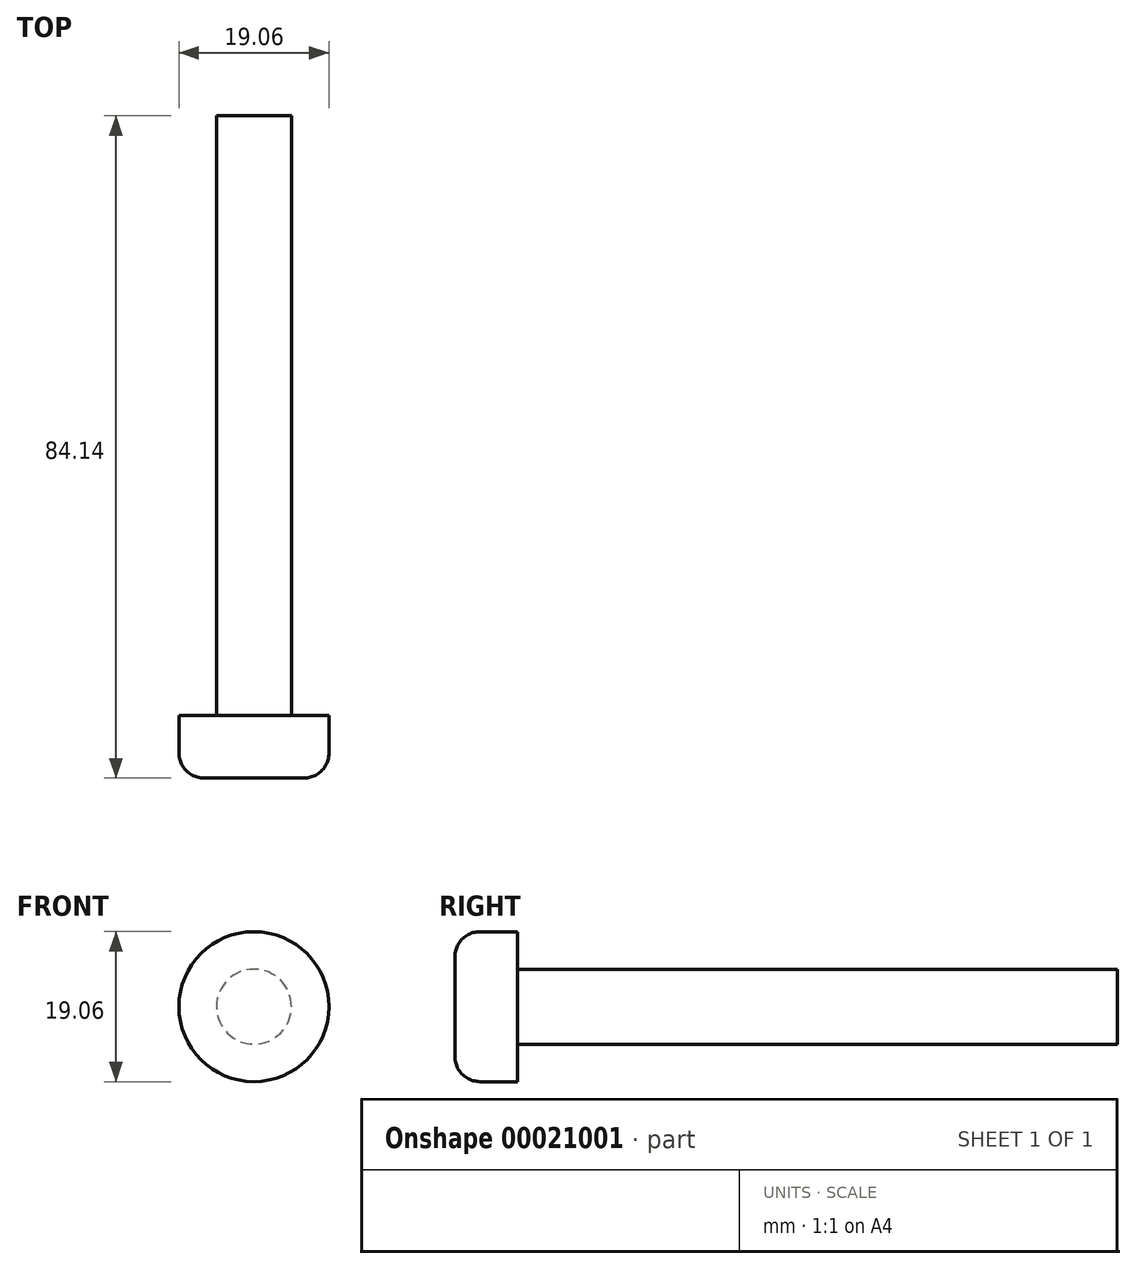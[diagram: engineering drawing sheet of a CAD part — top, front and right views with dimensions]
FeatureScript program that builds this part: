
annotation { "Feature Type Name" : "Feature", "Feature Type Description" : "" }
export const myFeature = defineFeature(function(context is Context, id is Id, definition is map)
    precondition{}
    {
        {
            var Q0;
            Q0=qCreatedBy(makeId("Front.planeOp"),FACE);
            var sketch = newSketch(context, id + "F0", { "sketchPlane" : qUnion([Q0])});
            skCircle(sketch, "E0", {"center": v(0, 0) * mm, "radius": 9.53 * mm});
            skSolve(sketch);
        }
        {
            var Q0;
            Q0=makeQuery(id+"F0.imprint","IMPRINT",FACE,{"disambiguationData":[TD([[makeQuery(id+"F0.imprint","IMPRINT",EDGE,{"derivedFrom":sQuery(id+"F0.wireOp",EDGE,"E0")}),1.0]])]});
            extrude(context, id + "F1", {"entities" : qUnion([Q0]), "depth" : 1.59 * mm});
        }
        {
            var Q0;
            Q0=qCreatedBy(makeId("Front.planeOp"),FACE);
            cPlane(context, id + "F2", {"entities" : qUnion([Q0]), "cplaneType" : CPlaneType.OFFSET, "offset" : 1.59 * mm, "width" : 152.4 * mm, "height" : 152.4 * mm});
        }
        {
            var Q0;
            Q0=qCreatedBy(id+"F2.planeOp",FACE);
            var sketch = newSketch(context, id + "F3", { "sketchPlane" : qUnion([Q0])});
            skCircle(sketch, "E1", {"center": v(0, 0) * mm, "radius": 9.53 * mm});
            skSolve(sketch);
        }
        {
            var Q0;
            Q0=makeQuery(id+"F3.imprint","IMPRINT",FACE,{"disambiguationData":[TD([[makeQuery(id+"F3.imprint","IMPRINT",EDGE,{"derivedFrom":sQuery(id+"F3.wireOp",EDGE,"E1")}),1.0]])]});
            extrude(context, id + "F4", {"entities" : qUnion([Q0]), "operationType" : NewBodyOperationType.ADD, "depth" : 6.35 * mm});
        }
        {
            var Q0;
            Q0=qCreatedBy(makeId("Front.planeOp"),FACE);
            var sketch = newSketch(context, id + "F5", { "sketchPlane" : qUnion([Q0])});
            skCircle(sketch, "E2", {"center": v(0, 0) * mm, "radius": 4.76 * mm});
            skSolve(sketch);
        }
        {
            var Q0;
            Q0=makeQuery(id+"F5.imprint","IMPRINT",FACE,{"disambiguationData":[TD([[makeQuery(id+"F5.imprint","IMPRINT",EDGE,{"derivedFrom":sQuery(id+"F5.wireOp",EDGE,"E2")}),1.0]])]});
            extrude(context, id + "F6", {"entities" : qUnion([Q0]), "oppositeDirection" : true, "depth" : 76.2 * mm});
        }
        {
            var Q0;
            Q0=makeQuery(id+"F4.opExtrude","CAP_EDGE",EDGE,{"disambiguationData":[OSD([sQuery(id+"F3.wireOp",EDGE,"E1")])],"isStart":false});
            fillet(context, id + "F7", {"entities" : qUnion([Q0]), "radius" : 3.17 * mm, "tangentPropagation" : true, "allowEdgeOverflow" : false});
        }
    });
